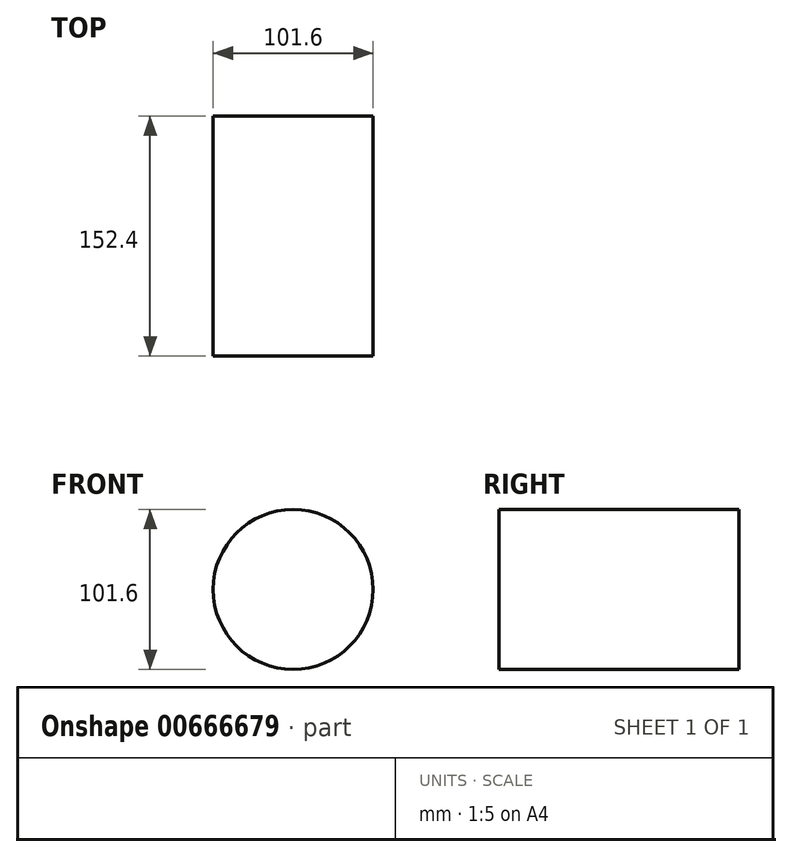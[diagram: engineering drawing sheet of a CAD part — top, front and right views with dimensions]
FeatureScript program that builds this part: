
annotation { "Feature Type Name" : "Feature", "Feature Type Description" : "" }
export const myFeature = defineFeature(function(context is Context, id is Id, definition is map)
    precondition{}
    {
        {
            var Q0;
            Q0=qCreatedBy(makeId("Front.planeOp"),FACE);
            var sketch = newSketch(context, id + "F0", { "sketchPlane" : qUnion([Q0])});
            skCircle(sketch, "E0", {"center": v(0, 0) * mm, "radius": 50.8 * mm});
            skSolve(sketch);
        }
        {
            var Q0;
            Q0 = qSketchRegion(id + "F0", false);
            extrude(context, id + "F1", {"entities" : qUnion([Q0]), "depth" : 152.4 * mm});
        }
    });
